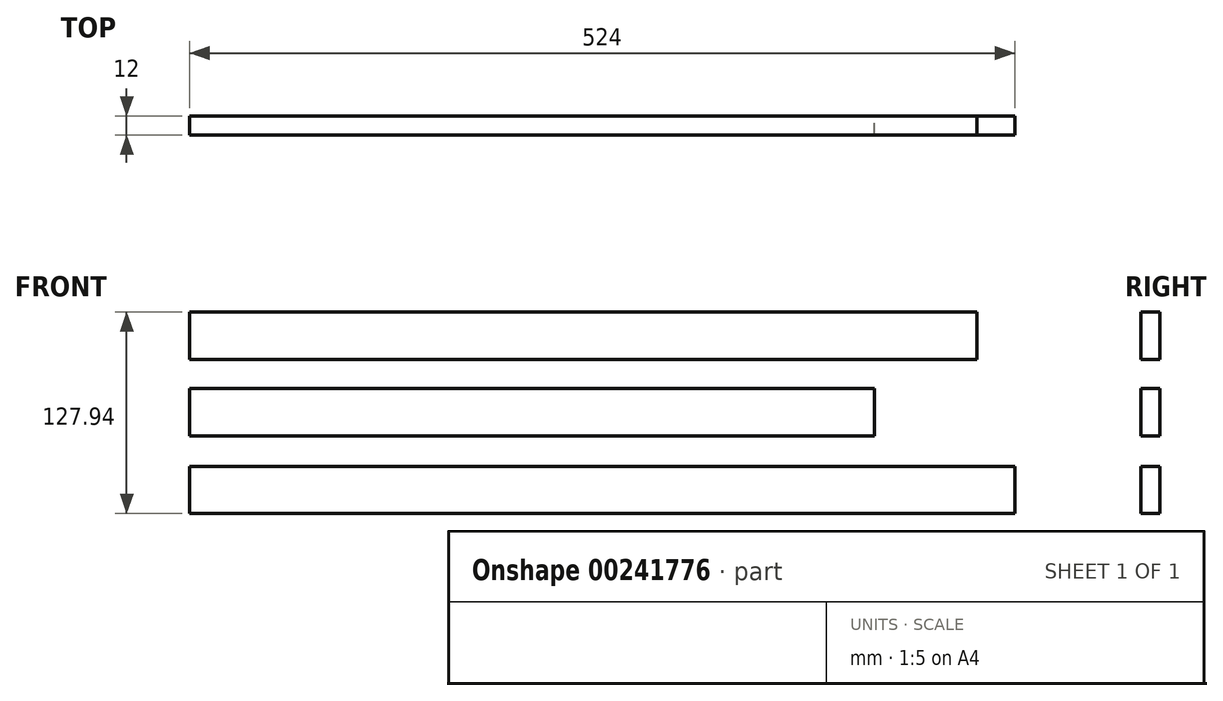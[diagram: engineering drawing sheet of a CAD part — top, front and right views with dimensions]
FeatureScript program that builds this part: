
annotation { "Feature Type Name" : "Feature", "Feature Type Description" : "" }
export const myFeature = defineFeature(function(context is Context, id is Id, definition is map)
    precondition{}
    {
        {
            var Q0;
            Q0=qCreatedBy(makeId("Front.planeOp"),FACE);
            var sketch = newSketch(context, id + "F0", { "sketchPlane" : qUnion([Q0])});
            skLineSegment(sketch, "E0.bottom", {"start": v(0, 0) * mm, "end": v(500, 0) * mm});
            skLineSegment(sketch, "E0.top", {"start": v(0, 30) * mm, "end": v(500, 30) * mm});
            skLineSegment(sketch, "E0.left", {"start": v(0, 0) * mm, "end": v(0, 30) * mm});
            skLineSegment(sketch, "E0.right", {"start": v(500, 0) * mm, "end": v(500, 30) * mm});
            skSolve(sketch);
        }
        {
            var Q0;
            Q0=qSketchRegion(id+"F0",true);
            extrude(context, id + "F1", {"entities" : qUnion([Q0]), "depth" : 12 * mm});
        }
        {
            var Q0;
            Q0=qCreatedBy(makeId("Front.planeOp"),FACE);
            var sketch = newSketch(context, id + "F2", { "sketchPlane" : qUnion([Q0])});
            skLineSegment(sketch, "E1.bottom", {"start": v(0, -48.56) * mm, "end": v(435, -48.56) * mm});
            skLineSegment(sketch, "E1.top", {"start": v(0, -18.56) * mm, "end": v(435, -18.56) * mm});
            skLineSegment(sketch, "E1.left", {"start": v(0, -48.56) * mm, "end": v(0, -18.56) * mm});
            skLineSegment(sketch, "E1.right", {"start": v(435, -48.56) * mm, "end": v(435, -18.56) * mm});
            skSolve(sketch);
        }
        {
            var Q0;
            Q0=makeQuery(id+"F2.imprint","IMPRINT",FACE,{"disambiguationData":[TD([[makeQuery(id+"F2.imprint","IMPRINT",EDGE,{"derivedFrom":sQuery(id+"F2.wireOp",EDGE,"E1.bottom")}),1.0]])]});
            extrude(context, id + "F3", {"entities" : qUnion([Q0]), "depth" : 12 * mm});
        }
        {
            var Q0;
            Q0=qCreatedBy(makeId("Front.planeOp"),FACE);
            var sketch = newSketch(context, id + "F4", { "sketchPlane" : qUnion([Q0])});
            skLineSegment(sketch, "E2.bottom", {"start": v(0, -97.94) * mm, "end": v(524, -97.94) * mm});
            skLineSegment(sketch, "E2.top", {"start": v(0, -67.94) * mm, "end": v(524, -67.94) * mm});
            skLineSegment(sketch, "E2.left", {"start": v(0, -97.94) * mm, "end": v(0, -67.94) * mm});
            skLineSegment(sketch, "E2.right", {"start": v(524, -97.94) * mm, "end": v(524, -67.94) * mm});
            skSolve(sketch);
        }
        {
            var Q0;
            Q0=makeQuery(id+"F4.imprint","IMPRINT",FACE,{"disambiguationData":[TD([[makeQuery(id+"F4.imprint","IMPRINT",EDGE,{"derivedFrom":sQuery(id+"F4.wireOp",EDGE,"E2.bottom")}),1.0]])]});
            extrude(context, id + "F5", {"entities" : qUnion([Q0]), "depth" : 12 * mm});
        }
    });
